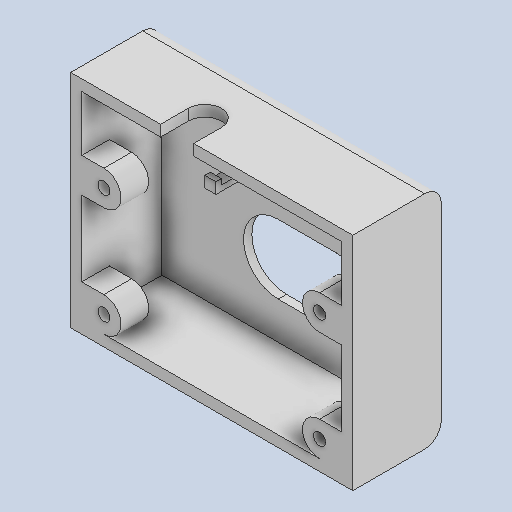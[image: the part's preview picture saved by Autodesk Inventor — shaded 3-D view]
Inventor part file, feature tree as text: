
AUTODESK INVENTOR PART (.ipt)
format: ipt  version: 2023.1 (Build 271208000, 208)  size: 402,944 bytes
history: native  units: mm
features: sketch x8, extrude x7, plane x3, fillet x1
ambient origin geometry x8: Origin, YZ Plane, XZ Plane, XY Plane, X Axis, Y Axis, Z Axis, Center Point
bodies: Solid1 (feature_tree)
feature tree (19):
  extrude  "Extrusion1"  Depth=51.0mm
  extrude  "Extrusion2"  Depth=2.0mm
  fillet  "Fillet1"  Radius=2.0mm
  extrude  "Extrusion3"  Depth=2.0mm
  sketch  "Sketch4"  dims[d8=14.5mm d9=0.0mm d10=3.0mm]
  plane  "Work Plane1"
  extrude  "Extrusion5"  Depth=3.0mm
  extrude  "Extrusion6"  Depth=14.0mm
  plane  "Work Plane2"
  extrude  "Extrusion9"  Depth=21.25mm
  plane  "Work Plane4"
  extrude  "Extrusion10"  TaperAngle=0.0deg  [1 undecoded]
  sketch  "Sketch1"  dims[d0=40.0mm d1=51.0mm]
  sketch  "Sketch2"  dims[d2=16.0mm d3=0.0mm d4=2.0mm d5=2.0mm]
  sketch  "Sketch3"  dims[d6=2.0mm d7=2.0mm]
  sketch  "Sketch5"  dims[d15=14.0mm d16=0.0mm d18=14.0mm]
  sketch  "Sketch6"  dims[d19=8.0mm d20=21.25mm]
  sketch  "Sketch10"  dims[d21=15.75mm d27=0.0mm]
  sketch  "Sketch12"  dims[d28=6.2mm d30=4.0mm d31=2.2mm d35=5.0mm d36=0.0mm d45=4.0mm d46=1.7mm d47=0.0mm d49=12.5mm d51=10.5mm d52=12.5mm d54=17.5mm d55=22.75mm d58=25.0mm d61=19.8mm d62=6.2mm d65=16.25mm d66=6.0mm d67=5.0mm d68=2.0mm d69=0.0mm d71=0.0mm d73=1.0mm d74=5.0mm d75=2.0mm d76=0.0mm d77=1.0mm d78=1.0mm d79=1.0mm d80=4.5mm d81=5.0mm d48=0.872665mm d59=0.0mm d60=0.0mm]
note: 1 required parameter value undecoded (feature->parameter linkage not recoverable at this tier; creation-order binding heuristic only, values carry confidence <= 0.55)
